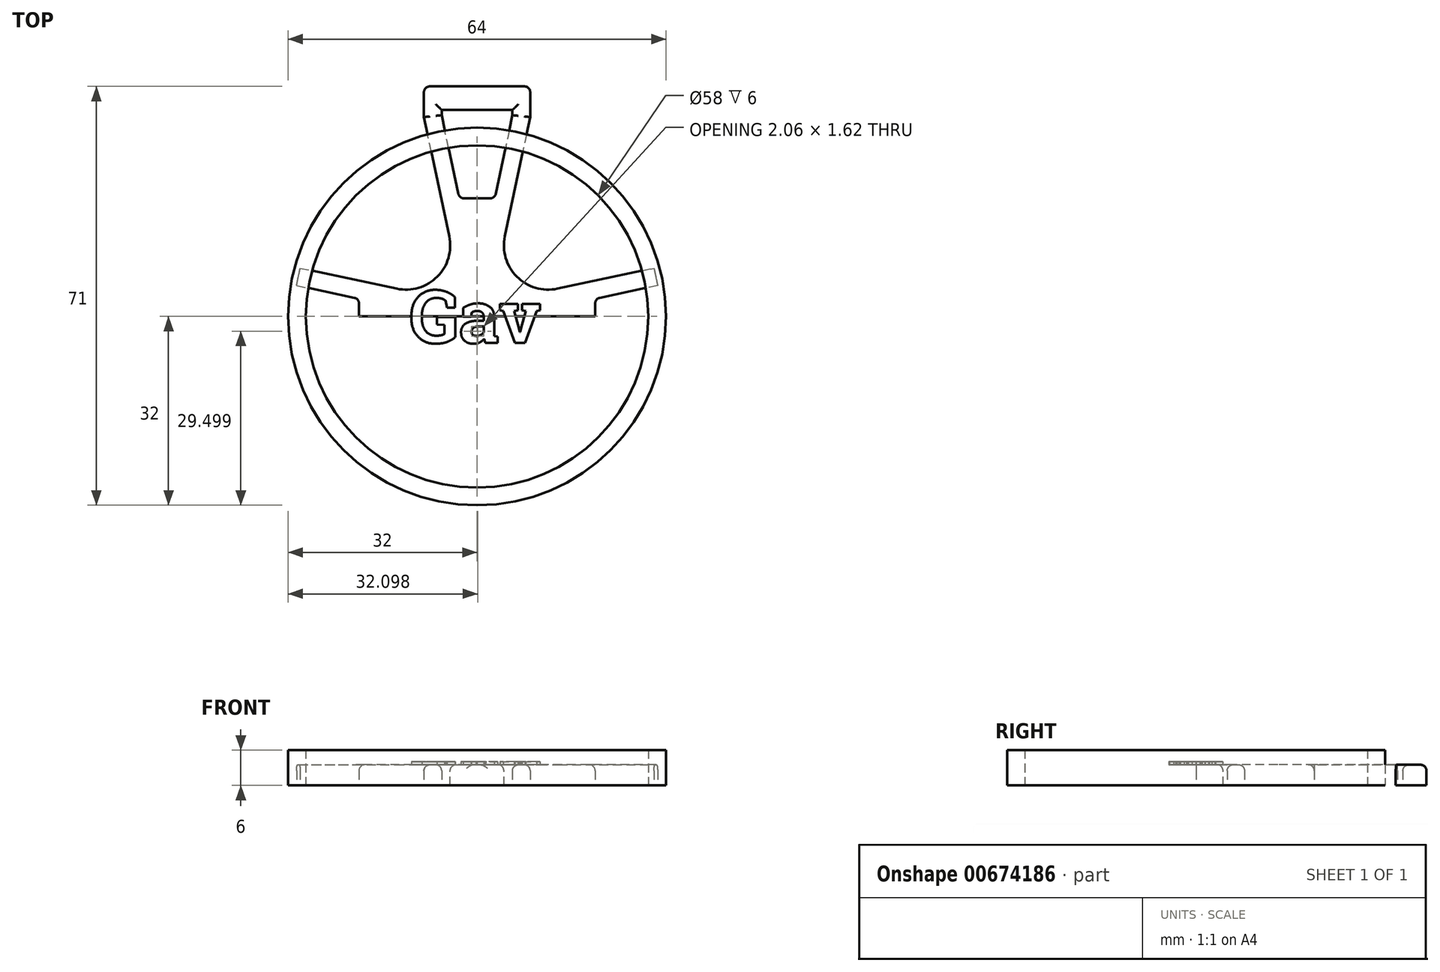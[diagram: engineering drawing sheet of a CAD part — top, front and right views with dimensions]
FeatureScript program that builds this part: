
annotation { "Feature Type Name" : "Feature", "Feature Type Description" : "" }
export const myFeature = defineFeature(function(context is Context, id is Id, definition is map)
    precondition{}
    {
        {
            var Q0;
            Q0=qCreatedBy(makeId("Top.planeOp"),FACE);
            var sketch = newSketch(context, id + "F0", { "sketchPlane" : qUnion([Q0])});
            skLineSegment(sketch, "E0", {"start": v(-9, 39) * mm, "end": v(9, 39) * mm});
            skLineSegment(sketch, "E1", {"start": v(9, 33.8) * mm, "end": v(2.3, 2.3) * mm});
            skLineSegment(sketch, "E2", {"start": v(2.3, 2.3) * mm, "end": v(29.95, 8.18) * mm});
            skLineSegment(sketch, "E3", {"start": v(-29.95, 8.18) * mm, "end": v(-2.3, 2.3) * mm});
            skLineSegment(sketch, "E4", {"start": v(-2.3, 2.3) * mm, "end": v(-9, 33.8) * mm});
            skLineSegment(sketch, "E5", {"start": v(-2.3, 2.3) * mm, "end": v(2.3, 2.3) * mm, "construction": true});
            skLineSegment(sketch, "E6.0", {"start": v(-3, 20) * mm, "end": v(-6, 34.11) * mm});
            skLineSegment(sketch, "E7", {"start": v(-3, 20) * mm, "end": v(3, 20) * mm});
            skLineSegment(sketch, "E8.trimOffspring", {"start": v(6, 34.11) * mm, "end": v(3, 20) * mm});
            skLineSegment(sketch, "E9", {"start": v(-6, 35) * mm, "end": v(6, 35) * mm});
            skLineSegment(sketch, "E10", {"start": v(-30.58, 5.25) * mm, "end": v(-20, 3) * mm});
            skLineSegment(sketch, "E11", {"start": v(-20, 3) * mm, "end": v(-20, 0) * mm});
            skLineSegment(sketch, "E12", {"start": v(20, 3) * mm, "end": v(20, 0) * mm});
            skLineSegment(sketch, "E13.trimOffspring", {"start": v(20, 0) * mm, "end": v(-20, 0) * mm});
            skCircle(sketch, "E14", {"center": v(0, 0) * mm, "radius": 32 * mm, "construction": true});
            skCircle(sketch, "E15", {"center": v(0, 0) * mm, "radius": 20 * mm, "construction": true});
            skLineSegment(sketch, "E16", {"start": v(-30.58, 5.25) * mm, "end": v(-29.95, 8.18) * mm});
            skLineSegment(sketch, "E17", {"start": v(-9, 39) * mm, "end": v(-9, 33.8) * mm});
            skLineSegment(sketch, "E18", {"start": v(-6, 35) * mm, "end": v(-6, 34.11) * mm});
            skLineSegment(sketch, "E19", {"start": v(6, 35) * mm, "end": v(6, 34.11) * mm});
            skLineSegment(sketch, "E20", {"start": v(9, 39) * mm, "end": v(9, 33.8) * mm});
            skLineSegment(sketch, "E21", {"start": v(29.95, 8.18) * mm, "end": v(30.58, 5.25) * mm});
            skLineSegment(sketch, "E22.trimOffspring", {"start": v(30.58, 5.25) * mm, "end": v(20, 3) * mm});
            skSolve(sketch);
        }
        {
            var Q0;
            Q0 = qSketchRegion(id + "F0", true);
            extrude(context, id + "F1", {"entities" : qUnion([Q0]), "depth" : 3.5 * mm, "offsetDistance" : 25 * mm});
        }
        {
            var Q0;
            Q0=makeQuery(id+"F1.opExtrude","SWEPT_EDGE",EDGE,{"disambiguationData":[OSD([sQuery(id+"F0.wireOp",EDGE,"E3"),sQuery(id+"F0.wireOp",EDGE,"E4")])]});
            var Q1;
            Q1=makeQuery(id+"F1.opExtrude","SWEPT_EDGE",EDGE,{"disambiguationData":[OSD([sQuery(id+"F0.wireOp",EDGE,"E1"),sQuery(id+"F0.wireOp",EDGE,"E2")])]});
            var Q2;
            Q2=makeQuery(id+"FIUa4nvhWZlZCv3_1.1.F1.opExtrude","SWEPT_EDGE",EDGE,{"disambiguationData":[OSD([sQuery(id+"F0.wireOp",EDGE,"E1"),sQuery(id+"F0.wireOp",EDGE,"E2")])]});
            var Q3;
            Q3=makeQuery(id+"FIUa4nvhWZlZCv3_1.1.F1.opExtrude","SWEPT_EDGE",EDGE,{"disambiguationData":[OSD([sQuery(id+"F0.wireOp",EDGE,"E3"),sQuery(id+"F0.wireOp",EDGE,"E4")])]});
            fillet(context, id + "F2", {"entities" : qUnion([Q0, Q1, Q2, Q3]), "radius" : 7.5 * mm, "tangentPropagation" : true, "allowEdgeOverflow" : false});
        }
        {
            var Q0;
            Q0=makeQuery(id+"F1.opExtrude","CAP_EDGE",EDGE,{"disambiguationData":[OSD([sQuery(id+"F0.wireOp",EDGE,"E6.0")])],"isStart":false});
            var Q1;
            Q1=makeQuery(id+"F1.opExtrude","CAP_EDGE",EDGE,{"disambiguationData":[OSD([sQuery(id+"F0.wireOp",EDGE,"E9")])],"isStart":false});
            var Q2;
            Q2=makeQuery(id+"F1.opExtrude","CAP_EDGE",EDGE,{"disambiguationData":[OSD([sQuery(id+"F0.wireOp",EDGE,"E8.trimOffspring")])],"isStart":false});
            var Q3;
            Q3=makeQuery(id+"F1.opExtrude","CAP_EDGE",EDGE,{"disambiguationData":[OSD([sQuery(id+"F0.wireOp",EDGE,"E17")])],"isStart":false});
            var Q4;
            Q4=makeQuery(id+"F1.opExtrude","CAP_EDGE",EDGE,{"disambiguationData":[OSD([sQuery(id+"F0.wireOp",EDGE,"E20")])],"isStart":false});
            var Q5;
            Q5=makeQuery(id+"F1.opExtrude","CAP_EDGE",EDGE,{"disambiguationData":[OSD([sQuery(id+"F0.wireOp",EDGE,"E2")])],"isStart":false});
            var Q6;
            Q6=makeQuery(id+"F1.opExtrude","CAP_EDGE",EDGE,{"disambiguationData":[OSD([sQuery(id+"F0.wireOp",EDGE,"E22.trimOffspring")])],"isStart":false});
            var Q7;
            Q7=makeQuery(id+"F1.opExtrude","CAP_EDGE",EDGE,{"disambiguationData":[OSD([sQuery(id+"F0.wireOp",EDGE,"E12")])],"isStart":false});
            var Q8;
            Q8=makeQuery(id+"F1.opExtrude","CAP_EDGE",EDGE,{"disambiguationData":[OSD([sQuery(id+"F0.wireOp",EDGE,"E3")])],"isStart":false});
            var Q9;
            Q9=makeQuery(id+"F1.opExtrude","CAP_EDGE",EDGE,{"disambiguationData":[OSD([sQuery(id+"F0.wireOp",EDGE,"E10")])],"isStart":false});
            var Q10;
            Q10=makeQuery(id+"F1.opExtrude","CAP_EDGE",EDGE,{"disambiguationData":[OSD([sQuery(id+"F0.wireOp",EDGE,"E11")])],"isStart":false});
            var Q11;
            Q11=makeQuery(id+"F1.opExtrude","SWEPT_EDGE",EDGE,{"disambiguationData":[OSD([sQuery(id+"F0.wireOp",EDGE,"E0"),sQuery(id+"F0.wireOp",EDGE,"E17")])]});
            var Q12;
            Q12=makeQuery(id+"F1.opExtrude","CAP_EDGE",EDGE,{"disambiguationData":[OSD([sQuery(id+"F0.wireOp",EDGE,"E19")])],"isStart":false});
            var Q13;
            Q13=makeQuery(id+"F1.opExtrude","CAP_EDGE",EDGE,{"disambiguationData":[OSD([sQuery(id+"F0.wireOp",EDGE,"E18")])],"isStart":false});
            var Q14;
            Q14=makeQuery(id+"FIUa4nvhWZlZCv3_1.1.F1.opExtrude","CAP_EDGE",EDGE,{"disambiguationData":[OSD([sQuery(id+"F0.wireOp",EDGE,"E3")])],"isStart":false});
            var Q15;
            Q15=makeQuery(id+"FIUa4nvhWZlZCv3_1.1.F1.opExtrude","CAP_EDGE",EDGE,{"disambiguationData":[OSD([sQuery(id+"F0.wireOp",EDGE,"E17")])],"isStart":false});
            var Q16;
            Q16=makeQuery(id+"FIUa4nvhWZlZCv3_1.1.F1.opExtrude","CAP_EDGE",EDGE,{"disambiguationData":[OSD([sQuery(id+"F0.wireOp",EDGE,"E0")])],"isStart":false});
            var Q17;
            Q17=makeQuery(id+"FIUa4nvhWZlZCv3_1.1.F1.opExtrude","CAP_EDGE",EDGE,{"disambiguationData":[OSD([sQuery(id+"F0.wireOp",EDGE,"E20")])],"isStart":false});
            var Q18;
            Q18=makeQuery(id+"FIUa4nvhWZlZCv3_1.1.F1.opExtrude","CAP_EDGE",EDGE,{"disambiguationData":[OSD([sQuery(id+"F0.wireOp",EDGE,"E8.trimOffspring")])],"isStart":false});
            var Q19;
            Q19=makeQuery(id+"FIUa4nvhWZlZCv3_1.1.F1.opExtrude","CAP_EDGE",EDGE,{"disambiguationData":[OSD([sQuery(id+"F0.wireOp",EDGE,"E7")])],"isStart":false});
            var Q20;
            Q20=makeQuery(id+"FIUa4nvhWZlZCv3_1.1.F1.opExtrude","CAP_EDGE",EDGE,{"disambiguationData":[OSD([sQuery(id+"F0.wireOp",EDGE,"E6.0")])],"isStart":false});
            var Q21;
            Q21=makeQuery(id+"FIUa4nvhWZlZCv3_1.1.F1.opExtrude","CAP_EDGE",EDGE,{"disambiguationData":[OSD([sQuery(id+"F0.wireOp",EDGE,"E9")])],"isStart":false});
            var Q22;
            Q22=makeQuery(id+"FIUa4nvhWZlZCv3_1.1.F1.opExtrude","CAP_EDGE",EDGE,{"disambiguationData":[OSD([sQuery(id+"F0.wireOp",EDGE,"E19")])],"isStart":false});
            var Q23;
            Q23=makeQuery(id+"FIUa4nvhWZlZCv3_1.1.F1.opExtrude","CAP_EDGE",EDGE,{"disambiguationData":[OSD([sQuery(id+"F0.wireOp",EDGE,"E18")])],"isStart":false});
            var Q24;
            Q24=makeQuery(id+"FIUa4nvhWZlZCv3_1.1.F1.opExtrude","CAP_EDGE",EDGE,{"disambiguationData":[OSD([sQuery(id+"F0.wireOp",EDGE,"E2")])],"isStart":false});
            var Q25;
            Q25=makeQuery(id+"FIUa4nvhWZlZCv3_1.1.F1.opExtrude","CAP_EDGE",EDGE,{"disambiguationData":[OSD([sQuery(id+"F0.wireOp",EDGE,"E22.trimOffspring")])],"isStart":false});
            var Q26;
            Q26=makeQuery(id+"FIUa4nvhWZlZCv3_1.1.F1.opExtrude","CAP_EDGE",EDGE,{"disambiguationData":[OSD([sQuery(id+"F0.wireOp",EDGE,"E12")])],"isStart":false});
            var Q27;
            Q27=makeQuery(id+"FIUa4nvhWZlZCv3_1.1.F1.opExtrude","SWEPT_EDGE",EDGE,{"disambiguationData":[OSD([sQuery(id+"F0.wireOp",EDGE,"E12"),sQuery(id+"F0.wireOp",EDGE,"E22.trimOffspring")])]});
            var Q28;
            Q28=makeQuery(id+"F1.opExtrude","SWEPT_EDGE",EDGE,{"disambiguationData":[OSD([sQuery(id+"F0.wireOp",EDGE,"E12"),sQuery(id+"F0.wireOp",EDGE,"E22.trimOffspring")])]});
            var Q29;
            Q29=makeQuery(id+"FIUa4nvhWZlZCv3_1.1.F1.opExtrude","SWEPT_EDGE",EDGE,{"disambiguationData":[OSD([sQuery(id+"F0.wireOp",EDGE,"E10"),sQuery(id+"F0.wireOp",EDGE,"E11")])]});
            var Q30;
            Q30=makeQuery(id+"F1.opExtrude","SWEPT_EDGE",EDGE,{"disambiguationData":[OSD([sQuery(id+"F0.wireOp",EDGE,"E10"),sQuery(id+"F0.wireOp",EDGE,"E11")])]});
            var Q31;
            Q31=makeQuery(id+"F1.opExtrude","SWEPT_EDGE",EDGE,{"disambiguationData":[OSD([sQuery(id+"F0.wireOp",EDGE,"E7"),sQuery(id+"F0.wireOp",EDGE,"E8.trimOffspring")])]});
            var Q32;
            Q32=makeQuery(id+"F1.opExtrude","SWEPT_EDGE",EDGE,{"disambiguationData":[OSD([sQuery(id+"F0.wireOp",EDGE,"E6.0"),sQuery(id+"F0.wireOp",EDGE,"E7")])]});
            var Q33;
            Q33=makeQuery(id+"FIUa4nvhWZlZCv3_1.1.F1.opExtrude","CAP_EDGE",EDGE,{"disambiguationData":[OSD([sQuery(id+"F0.wireOp",EDGE,"E11")])],"isStart":false});
            var Q34;
            Q34=makeQuery(id+"F1.opExtrude","CAP_EDGE",EDGE,{"disambiguationData":[OSD([sQuery(id+"F0.wireOp",EDGE,"E0")])],"isStart":false});
            var Q35;
            Q35=makeQuery(id+"FIUa4nvhWZlZCv3_1.1.F1.opExtrude","SWEPT_EDGE",EDGE,{"disambiguationData":[OSD([sQuery(id+"F0.wireOp",EDGE,"E0"),sQuery(id+"F0.wireOp",EDGE,"E20")])]});
            var Q36;
            Q36=makeQuery(id+"FIUa4nvhWZlZCv3_1.1.F1.opExtrude","SWEPT_EDGE",EDGE,{"disambiguationData":[OSD([sQuery(id+"F0.wireOp",EDGE,"E0"),sQuery(id+"F0.wireOp",EDGE,"E17")])]});
            var Q37;
            Q37=makeQuery(id+"F1.opExtrude","SWEPT_EDGE",EDGE,{"disambiguationData":[OSD([sQuery(id+"F0.wireOp",EDGE,"E0"),sQuery(id+"F0.wireOp",EDGE,"E20")])]});
            var Q38;
            Q38=makeQuery(id+"FIUa4nvhWZlZCv3_1.1.F1.opExtrude","SWEPT_EDGE",EDGE,{"disambiguationData":[OSD([sQuery(id+"F0.wireOp",EDGE,"E6.0"),sQuery(id+"F0.wireOp",EDGE,"E7")])]});
            var Q39;
            Q39=makeQuery(id+"FIUa4nvhWZlZCv3_1.1.F1.opExtrude","SWEPT_EDGE",EDGE,{"disambiguationData":[OSD([sQuery(id+"F0.wireOp",EDGE,"E7"),sQuery(id+"F0.wireOp",EDGE,"E8.trimOffspring")])]});
            fillet(context, id + "F3", {"entities" : qUnion([Q0, Q1, Q2, Q3, Q4, Q5, Q6, Q7, Q8, Q9, Q10, Q11, Q12, Q13, Q14, Q15, Q16, Q17, Q18, Q19, Q20, Q21, Q22, Q23, Q24, Q25, Q26, Q27, Q28, Q29, Q30, Q31, Q32, Q33, Q34, Q35, Q36, Q37, Q38, Q39]), "radius" : 1 * mm, "tangentPropagation" : true, "allowEdgeOverflow" : false});
        }
        {
            var Q0;
            Q0=qCreatedBy(makeId("Top.planeOp"),FACE);
            var sketch = newSketch(context, id + "F4", { "sketchPlane" : qUnion([Q0])});
            skCircle(sketch, "E23", {"center": v(0, 0) * mm, "radius": 32 * mm});
            skCircle(sketch, "E24", {"center": v(0, 0) * mm, "radius": 29 * mm});
            skSolve(sketch);
        }
        {
            var Q0;
            Q0 = qSketchRegion(id + "F4", true);
            extrude(context, id + "F5", {"entities" : qUnion([Q0]), "depth" : 6 * mm, "offsetDistance" : 25 * mm});
        }
        {
            var Q0;
            Q0=makeQuery(id+"F3.opFillet","SPLIT",FACE,{"disambiguationData":[OD(0.0)],"derivedFrom":makeQuery(id+"F1.opExtrude","CAP_FACE",FACE,{"disambiguationData":[OSD([sQuery(id+"F0.wireOp",EDGE,"E0"),sQuery(id+"F0.wireOp",EDGE,"E1"),sQuery(id+"F0.wireOp",EDGE,"E2"),sQuery(id+"F0.wireOp",EDGE,"E3"),sQuery(id+"F0.wireOp",EDGE,"E4"),sQuery(id+"F0.wireOp",EDGE,"E6.0"),sQuery(id+"F0.wireOp",EDGE,"E7"),sQuery(id+"F0.wireOp",EDGE,"E8.trimOffspring"),sQuery(id+"F0.wireOp",EDGE,"E9"),sQuery(id+"F0.wireOp",EDGE,"E10"),sQuery(id+"F0.wireOp",EDGE,"E11"),sQuery(id+"F0.wireOp",EDGE,"E12"),sQuery(id+"F0.wireOp",EDGE,"E13.trimOffspring"),sQuery(id+"F0.wireOp",EDGE,"E16"),sQuery(id+"F0.wireOp",EDGE,"E17"),sQuery(id+"F0.wireOp",EDGE,"E18"),sQuery(id+"F0.wireOp",EDGE,"E19"),sQuery(id+"F0.wireOp",EDGE,"E20"),sQuery(id+"F0.wireOp",EDGE,"E21"),sQuery(id+"F0.wireOp",EDGE,"E22.trimOffspring")])],"isStart":false})});
            var sketch = newSketch(context, id + "F6", { "sketchPlane" : qUnion([Q0])});
            skText(sketch, "E25", { "text": "Gav", "fontName": "RobotoSlab-Bold.ttf"});
            const initialGuessF6  = {"E25": [-0.01142, -0.0045, 1, 0, 0.009]};
            skSetInitialGuess(sketch, initialGuessF6);
            skSolve(sketch);
        }
        {
            var Q0;
            Q0 = qSketchRegion(id + "F6", true);
            extrude(context, id + "F7", {"entities" : qUnion([Q0]), "depth" : .5 * mm, "offsetDistance" : 25 * mm});
        }
    });
